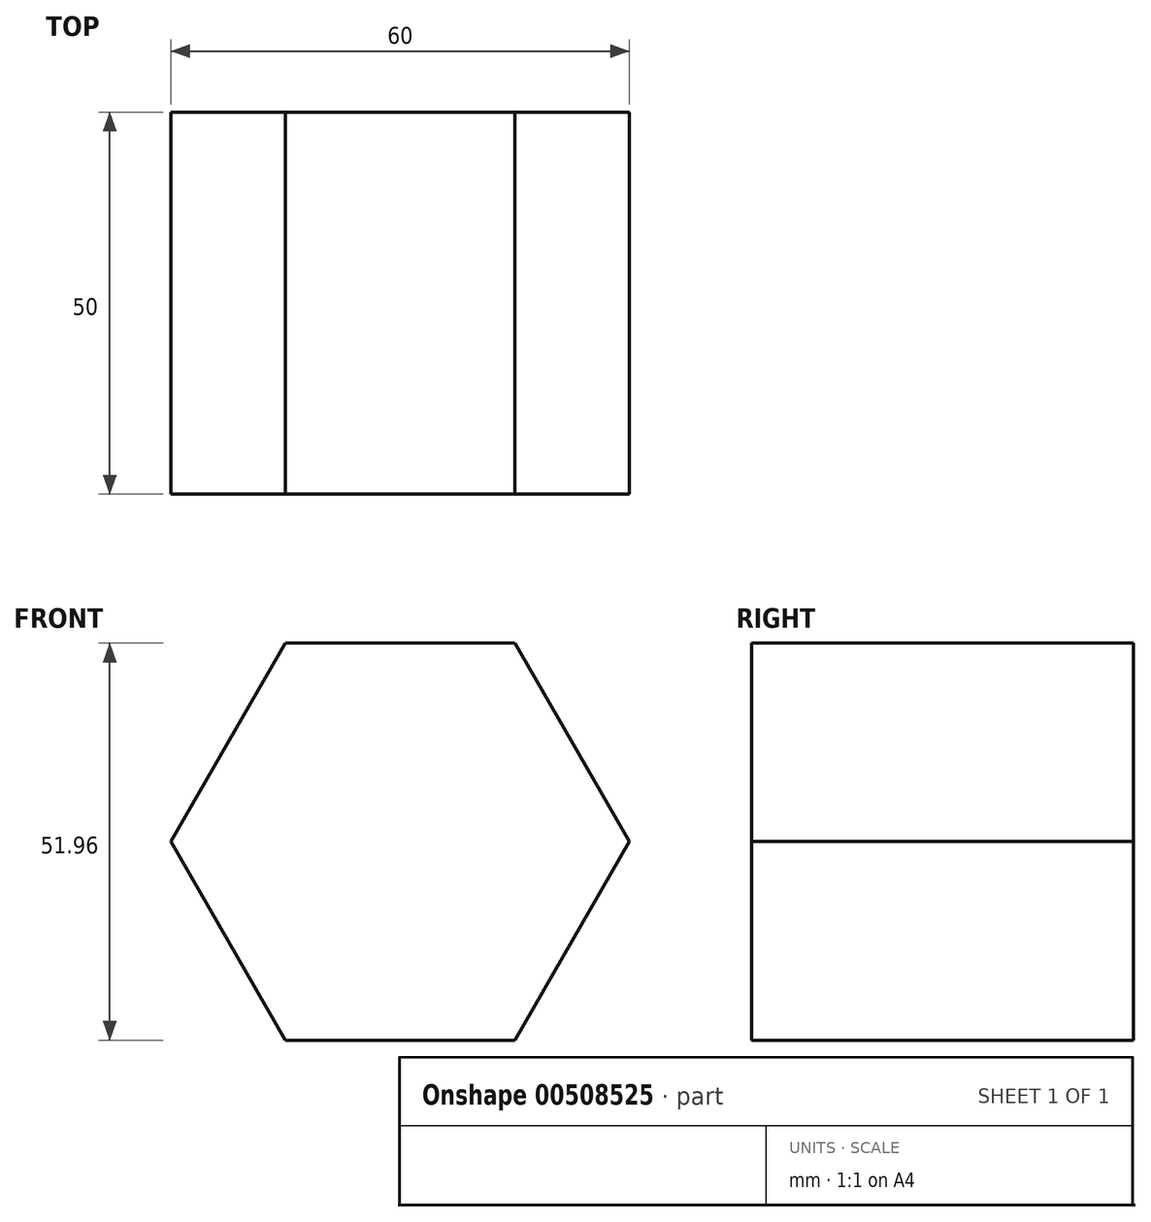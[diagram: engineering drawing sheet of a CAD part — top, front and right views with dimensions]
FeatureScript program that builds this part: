
annotation { "Feature Type Name" : "Feature", "Feature Type Description" : "" }
export const myFeature = defineFeature(function(context is Context, id is Id, definition is map)
    precondition{}
    {
        {
            var Q0;
            Q0=qCreatedBy(makeId("Front.planeOp"),FACE);
            var sketch = newSketch(context, id + "F0", { "sketchPlane" : qUnion([Q0])});
            skCircle(sketch, "E0.cCircle", {"center": v(0, 0) * mm, "radius": 30 * mm, "construction": true});
            skLineSegment(sketch, "E0.0", {"start": v(30, 0) * mm, "end": v(15, -25.98) * mm});
            skLineSegment(sketch, "E0.1", {"start": v(15, -25.98) * mm, "end": v(-15, -25.98) * mm});
            skLineSegment(sketch, "E0.2", {"start": v(-15, -25.98) * mm, "end": v(-30, 0) * mm});
            skLineSegment(sketch, "E0.3", {"start": v(-30, 0) * mm, "end": v(-15, 25.98) * mm});
            skLineSegment(sketch, "E0.4", {"start": v(-15, 25.98) * mm, "end": v(15, 25.98) * mm});
            skLineSegment(sketch, "E0.5", {"start": v(15, 25.98) * mm, "end": v(30, 0) * mm});
            skSolve(sketch);
        }
        {
            var Q0;
            Q0=qSketchRegion(id+"F0",true);
            extrude(context, id + "F1", {"entities" : qUnion([Q0]), "depth" : 50 * mm});
        }
    });
